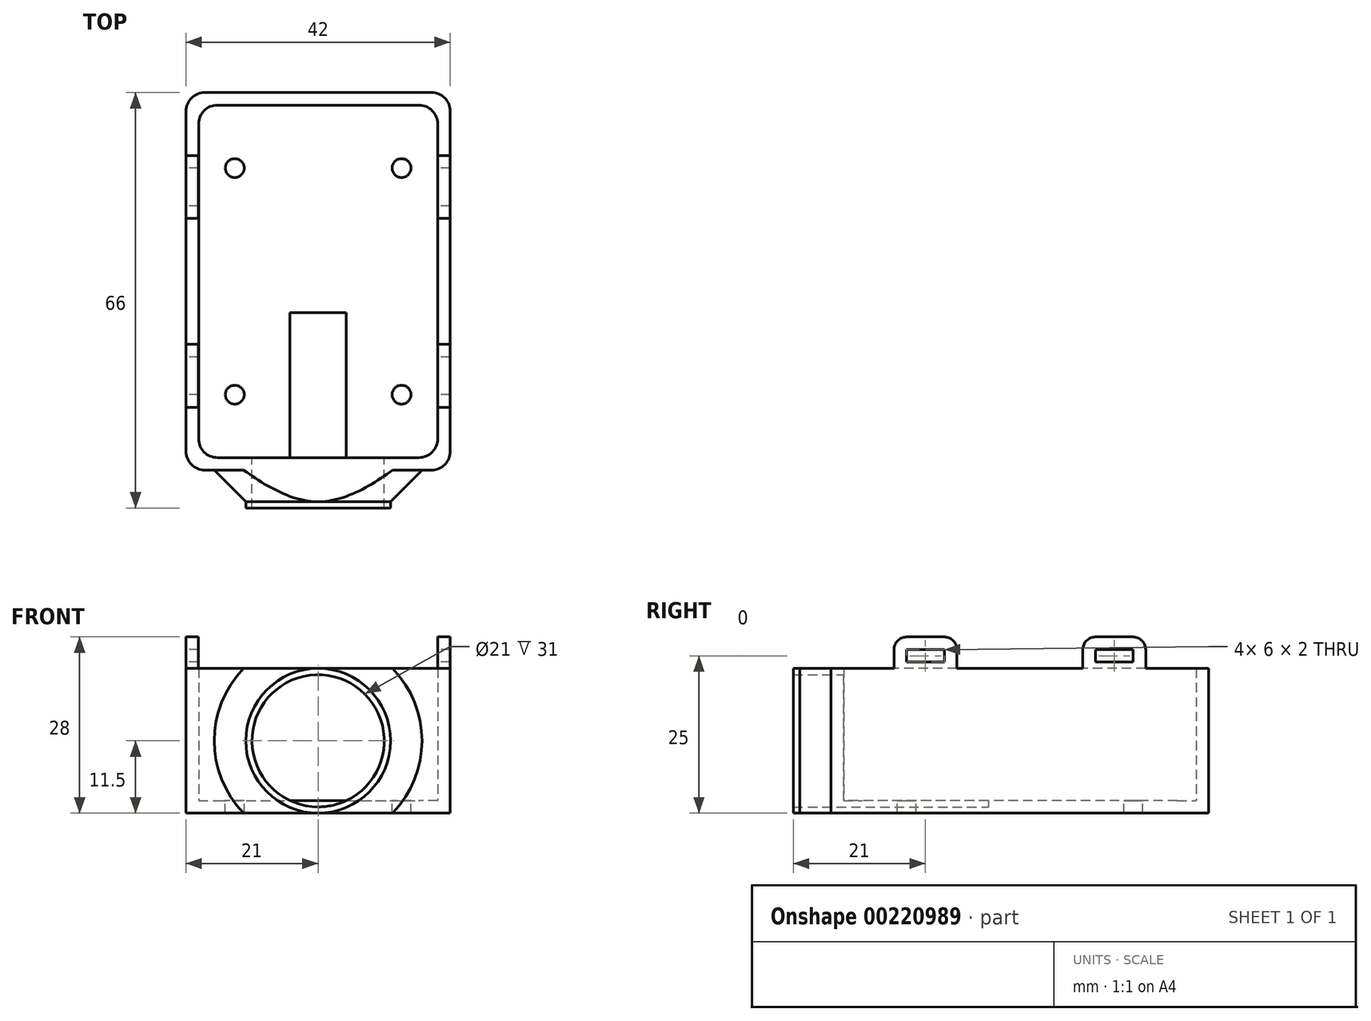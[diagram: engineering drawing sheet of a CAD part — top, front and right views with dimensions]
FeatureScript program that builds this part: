
annotation { "Feature Type Name" : "Feature", "Feature Type Description" : "" }
export const myFeature = defineFeature(function(context is Context, id is Id, definition is map)
    precondition{}
    {
        {
            assignVariable(context, id + "F0", {"name" : "defaultThickness", "anyValue" : 2});
        }
        {
            assignVariable(context, id + "F1", {"name" : "depth", "anyValue" : 21});
        }
        {
            assignVariable(context, id + "F2", {"name" : "camProtrusion", "anyValue" : 12});
        }
        {
            var Q0;
            Q0=qCreatedBy(makeId("Top.planeOp"),FACE);
            var sketch = newSketch(context, id + "F3", { "sketchPlane" : qUnion([Q0])});
            skLineSegment(sketch, "E0.bottom", {"start": v(-16, 28) * mm, "end": v(16, 28) * mm});
            skLineSegment(sketch, "E0.top", {"start": v(-16, -28) * mm, "end": v(16, -28) * mm});
            skLineSegment(sketch, "E0.left", {"start": v(-19, 25) * mm, "end": v(-19, -25) * mm});
            skLineSegment(sketch, "E0.right", {"start": v(19, 25) * mm, "end": v(19, -25) * mm});
            skPoint(sketch, "E0.middle", {"position": v(0, 0) * mm});
            skLineSegment(sketch, "E1.bottom", {"start": v(-18, 30) * mm, "end": v(18, 30) * mm});
            skLineSegment(sketch, "E1.top", {"start": v(-18, -30) * mm, "end": v(18, -30) * mm});
            skLineSegment(sketch, "E1.left", {"start": v(-21, 27) * mm, "end": v(-21, -27) * mm});
            skLineSegment(sketch, "E1.right", {"start": v(21, 27) * mm, "end": v(21, -27) * mm});
            skPoint(sketch, "E2.visualSharp", {"position": v(-19, 28) * mm});
            skArc(sketch, "E2.filletArc", {"start": v(-16, 28) * mm, "mid": v(-18.12, 27.12) * mm, "end": v(-19, 25) * mm});
            skPoint(sketch, "E3.visualSharp", {"position": v(19, 28) * mm});
            skArc(sketch, "E3.filletArc", {"start": v(19, 25) * mm, "mid": v(18.12, 27.12) * mm, "end": v(16, 28) * mm});
            skPoint(sketch, "E4.visualSharp", {"position": v(19, -28) * mm});
            skArc(sketch, "E4.filletArc", {"start": v(16, -28) * mm, "mid": v(18.12, -27.12) * mm, "end": v(19, -25) * mm});
            skPoint(sketch, "E5.visualSharp", {"position": v(-19, -28) * mm});
            skArc(sketch, "E5.filletArc", {"start": v(-19, -25) * mm, "mid": v(-18.12, -27.12) * mm, "end": v(-16, -28) * mm});
            skPoint(sketch, "E6.visualSharp", {"position": v(-21, -30) * mm});
            skArc(sketch, "E6.filletArc", {"start": v(-21, -27) * mm, "mid": v(-20.12, -29.12) * mm, "end": v(-18, -30) * mm});
            skPoint(sketch, "E7.visualSharp", {"position": v(21, -30) * mm});
            skArc(sketch, "E7.filletArc", {"start": v(18, -30) * mm, "mid": v(20.12, -29.12) * mm, "end": v(21, -27) * mm});
            skPoint(sketch, "E8.visualSharp", {"position": v(21, 30) * mm});
            skArc(sketch, "E8.filletArc", {"start": v(21, 27) * mm, "mid": v(20.12, 29.12) * mm, "end": v(18, 30) * mm});
            skPoint(sketch, "E9.visualSharp", {"position": v(-21, 30) * mm});
            skArc(sketch, "E9.filletArc", {"start": v(-18, 30) * mm, "mid": v(-20.12, 29.12) * mm, "end": v(-21, 27) * mm});
            skSolve(sketch);
        }
        {
            var Q0;
            Q0=makeQuery(id+"F3.imprint","IMPRINT",FACE,{"disambiguationData":[TD([[makeQuery(id+"F3.imprint","IMPRINT",EDGE,{"derivedFrom":sQuery(id+"F3.wireOp",EDGE,"E0.bottom")}),1.0]])]});
            extrude(context, id + "F4", {"entities" : qUnion([Q0]), "depth" : (getVariable(context, 'depth') + getVariable(context, 'defaultThickness')) * mm});
        }
        {
            var Q0;
            Q0=makeQuery(id+"F3.imprint","IMPRINT",FACE,{"disambiguationData":[TD([[makeQuery(id+"F3.imprint","IMPRINT",EDGE,{"derivedFrom":sQuery(id+"F3.wireOp",EDGE,"E0.bottom")}),-1.0]])]});
            extrude(context, id + "F5", {"entities" : qUnion([Q0]), "operationType" : NewBodyOperationType.ADD, "depth" : (getVariable(context, 'defaultThickness')) * mm});
        }
        {
            var Q0;
            Q0=makeQuery(id+"F4.opExtrude","SWEPT_FACE",FACE,{"disambiguationData":[OSD([sQuery(id+"F3.wireOp",EDGE,"E1.top")])]});
            var sketch = newSketch(context, id + "F6", { "sketchPlane" : qUnion([Q0])});
            skCircle(sketch, "E10", {"center": v(0, 11.5) * mm, "radius": 10.5 * mm});
            skCircle(sketch, "E11", {"center": v(0, 11.5) * mm, "radius": 11.5 * mm});
            skSolve(sketch);
        }
        {
            var Q0;
            Q0 = qSketchRegion(id + "F6", true);
            extrude(context, id + "F7", {"entities" : qUnion([Q0]), "operationType" : NewBodyOperationType.ADD, "depth" : (getVariable(context, 'camProtrusion') / 2) * mm});
        }
        {
            var Q0;
            Q0=makeQuery(id+"F7.boolean.opBoolean","SPLIT",FACE,{"disambiguationData":[TD([makeQuery(id+"F7.opExtrude","SWEPT_FACE",FACE,{"disambiguationData":[OSD([sQuery(id+"F6.wireOp",EDGE,"E10")])]})])],"derivedFrom":makeQuery(id+"F4.opExtrude","SWEPT_FACE",FACE,{"disambiguationData":[OSD([sQuery(id+"F3.wireOp",EDGE,"E1.top")])]})});
            extrude(context, id + "F8", {"entities" : qUnion([Q0]), "operationType" : NewBodyOperationType.REMOVE, "oppositeDirection" : true, "depth" : 25 * mm});
        }
        {
            var Q0;
            Q0=makeQuery(id+"F7.boolean.opBoolean","SPLIT",EDGE,{"disambiguationData":[OD(1.0)],"derivedFrom":makeQuery(id+"F7.opExtrude","CAP_EDGE",EDGE,{"disambiguationData":[OSD([sQuery(id+"F6.wireOp",EDGE,"E11")])],"isStart":true})});
            chamfer(context, id + "F9", {"entities" : qUnion([Q0]), "width" : 5 * mm, "tangentPropagation" : true});
        }
        {
            var Q0;
            Q0=makeQuery(id+"F5.opExtrude","CAP_FACE",FACE,{"disambiguationData":[OSD([sQuery(id+"F3.wireOp",EDGE,"E0.bottom"),sQuery(id+"F3.wireOp",EDGE,"E0.top"),sQuery(id+"F3.wireOp",EDGE,"E0.left"),sQuery(id+"F3.wireOp",EDGE,"E0.right"),sQuery(id+"F3.wireOp",EDGE,"E2.filletArc"),sQuery(id+"F3.wireOp",EDGE,"E3.filletArc"),sQuery(id+"F3.wireOp",EDGE,"E4.filletArc"),sQuery(id+"F3.wireOp",EDGE,"E5.filletArc")])],"isStart":false});
            var sketch = newSketch(context, id + "F10", { "sketchPlane" : qUnion([Q0])});
            skCircle(sketch, "E12", {"center": v(-13.25, 18) * mm, "radius": 1.5 * mm});
            skCircle(sketch, "E13", {"center": v(-13.25, -18) * mm, "radius": 1.5 * mm});
            skCircle(sketch, "E14", {"center": v(13.25, 18) * mm, "radius": 1.5 * mm});
            skCircle(sketch, "E15", {"center": v(13.25, -18) * mm, "radius": 1.5 * mm});
            skPoint(sketch, "E16", {"position": v(-0.21, -18) * mm});
            skLineSegment(sketch, "E17", {"start": v(-13.25, 18) * mm, "end": v(0, 18) * mm, "construction": true});
            skLineSegment(sketch, "E18", {"start": v(0, 18) * mm, "end": v(13.25, 18) * mm, "construction": true});
            skLineSegment(sketch, "E19", {"start": v(-13.25, -18) * mm, "end": v(0, -18) * mm, "construction": true});
            skLineSegment(sketch, "E20", {"start": v(0, -18) * mm, "end": v(13.25, -18) * mm, "construction": true});
            skSolve(sketch);
        }
        {
            var Q0;
            Q0 = qSketchRegion(id + "F10", true);
            extrude(context, id + "F11", {"entities" : qUnion([Q0]), "operationType" : NewBodyOperationType.REMOVE, "endBound" : BoundingType.THROUGH_ALL, "oppositeDirection" : true, "depth" : 25 * mm});
        }
        {
            var Q0;
            Q0=makeQuery(id+"F4.opExtrude","CAP_FACE",FACE,{"disambiguationData":[OSD([sQuery(id+"F3.wireOp",EDGE,"E0.bottom"),sQuery(id+"F3.wireOp",EDGE,"E0.top"),sQuery(id+"F3.wireOp",EDGE,"E0.left"),sQuery(id+"F3.wireOp",EDGE,"E0.right"),sQuery(id+"F3.wireOp",EDGE,"E1.bottom"),sQuery(id+"F3.wireOp",EDGE,"E1.top"),sQuery(id+"F3.wireOp",EDGE,"E1.left"),sQuery(id+"F3.wireOp",EDGE,"E1.right"),sQuery(id+"F3.wireOp",EDGE,"E2.filletArc"),sQuery(id+"F3.wireOp",EDGE,"E3.filletArc"),sQuery(id+"F3.wireOp",EDGE,"E4.filletArc"),sQuery(id+"F3.wireOp",EDGE,"E5.filletArc"),sQuery(id+"F3.wireOp",EDGE,"E6.filletArc"),sQuery(id+"F3.wireOp",EDGE,"E7.filletArc"),sQuery(id+"F3.wireOp",EDGE,"E8.filletArc"),sQuery(id+"F3.wireOp",EDGE,"E9.filletArc")])],"isStart":false});
            var sketch = newSketch(context, id + "F12", { "sketchPlane" : qUnion([Q0])});
            skLineSegment(sketch, "E21.bottom", {"start": v(-21, 20) * mm, "end": v(-19.01, 20) * mm});
            skLineSegment(sketch, "E21.top", {"start": v(-21, 10) * mm, "end": v(-19.01, 10) * mm});
            skLineSegment(sketch, "E21.left", {"start": v(-21, 20) * mm, "end": v(-21, 10) * mm});
            skLineSegment(sketch, "E21.right", {"start": v(-19.01, 20) * mm, "end": v(-19.01, 10) * mm});
            skPoint(sketch, "E21.middle", {"position": v(-20, 15) * mm});
            skLineSegment(sketch, "E22.bottom", {"start": v(-21, -10) * mm, "end": v(-19.01, -10) * mm});
            skLineSegment(sketch, "E22.top", {"start": v(-21, -20) * mm, "end": v(-19.01, -20) * mm});
            skLineSegment(sketch, "E22.left", {"start": v(-21, -10) * mm, "end": v(-21, -20) * mm});
            skLineSegment(sketch, "E22.right", {"start": v(-19.01, -10) * mm, "end": v(-19.01, -20) * mm});
            skPoint(sketch, "E22.middle", {"position": v(-20, -15) * mm});
            skLineSegment(sketch, "E23", {"start": v(-20, 15) * mm, "end": v(-20, 0) * mm, "construction": true});
            skLineSegment(sketch, "E24", {"start": v(-20, 0) * mm, "end": v(-20, -15) * mm, "construction": true});
            skLineSegment(sketch, "E25.MirrorCS", {"start": v(21, 20) * mm, "end": v(21, 10) * mm});
            skLineSegment(sketch, "E26.MirrorCS", {"start": v(21, 20) * mm, "end": v(19.01, 20) * mm});
            skLineSegment(sketch, "E27.MirrorCS", {"start": v(21, -20) * mm, "end": v(19.01, -20) * mm});
            skLineSegment(sketch, "E28.MirrorCS", {"start": v(21, 10) * mm, "end": v(19.01, 10) * mm});
            skLineSegment(sketch, "E29.MirrorCS", {"start": v(21, -10) * mm, "end": v(19.01, -10) * mm});
            skPoint(sketch, "E30.MirrorP", {"position": v(20, 15) * mm});
            skLineSegment(sketch, "E31.MirrorCS", {"start": v(20, 0) * mm, "end": v(20, -15) * mm, "construction": true});
            skLineSegment(sketch, "E32.MirrorCS", {"start": v(20, 15) * mm, "end": v(20, 0) * mm, "construction": true});
            skLineSegment(sketch, "E33.MirrorCS", {"start": v(19.01, -10) * mm, "end": v(19.01, -20) * mm});
            skLineSegment(sketch, "E34.MirrorCS", {"start": v(21, -10) * mm, "end": v(21, -20) * mm});
            skPoint(sketch, "E35.MirrorP", {"position": v(20, -15) * mm});
            skLineSegment(sketch, "E36.MirrorCS", {"start": v(19.01, 20) * mm, "end": v(19.01, 10) * mm});
            skSolve(sketch);
        }
        {
            var Q0;
            Q0 = qSketchRegion(id + "F12", true);
            extrude(context, id + "F13", {"entities" : qUnion([Q0]), "operationType" : NewBodyOperationType.ADD, "depth" : 5 * mm});
        }
        {
            var Q0;
            Q0=makeQuery(id+"F13.opExtrude","CAP_EDGE",EDGE,{"disambiguationData":[OSD([sQuery(id+"F12.wireOp",EDGE,"E22.top")])],"isStart":false});
            var Q1;
            Q1=makeQuery(id+"F13.opExtrude","CAP_EDGE",EDGE,{"disambiguationData":[OSD([sQuery(id+"F12.wireOp",EDGE,"E22.bottom")])],"isStart":false});
            var Q2;
            Q2=makeQuery(id+"F13.opExtrude","CAP_EDGE",EDGE,{"disambiguationData":[OSD([sQuery(id+"F12.wireOp",EDGE,"E21.top")])],"isStart":false});
            var Q3;
            Q3=makeQuery(id+"F13.opExtrude","CAP_EDGE",EDGE,{"disambiguationData":[OSD([sQuery(id+"F12.wireOp",EDGE,"E21.bottom")])],"isStart":false});
            var Q4;
            Q4=makeQuery(id+"F13.opExtrude","CAP_EDGE",EDGE,{"disambiguationData":[OSD([sQuery(id+"F12.wireOp",EDGE,"E26.MirrorCS")])],"isStart":false});
            var Q5;
            Q5=makeQuery(id+"F13.opExtrude","CAP_EDGE",EDGE,{"disambiguationData":[OSD([sQuery(id+"F12.wireOp",EDGE,"E28.MirrorCS")])],"isStart":false});
            var Q6;
            Q6=makeQuery(id+"F13.opExtrude","CAP_EDGE",EDGE,{"disambiguationData":[OSD([sQuery(id+"F12.wireOp",EDGE,"E29.MirrorCS")])],"isStart":false});
            var Q7;
            Q7=makeQuery(id+"F13.opExtrude","CAP_EDGE",EDGE,{"disambiguationData":[OSD([sQuery(id+"F12.wireOp",EDGE,"E27.MirrorCS")])],"isStart":false});
            fillet(context, id + "F14", {"entities" : qUnion([Q0, Q1, Q2, Q3, Q4, Q5, Q6, Q7]), "radius" : 2 * mm, "tangentPropagation" : true, "allowEdgeOverflow" : false});
        }
        {
            var Q0;
            Q0=makeQuery(id+"F13.boolean.opBoolean","MERGE",FACE,{"derivedFrom":[makeQuery(id+"F4.opExtrude","SWEPT_FACE",FACE,{"disambiguationData":[OSD([sQuery(id+"F3.wireOp",EDGE,"E1.left")])]}),makeQuery(id+"F13.opExtrude","SWEPT_FACE",FACE,{"disambiguationData":[OSD([sQuery(id+"F12.wireOp",EDGE,"E21.left")])]}),makeQuery(id+"F13.opExtrude","SWEPT_FACE",FACE,{"disambiguationData":[OSD([sQuery(id+"F12.wireOp",EDGE,"E22.left")])]})]});
            var sketch = newSketch(context, id + "F15", { "sketchPlane" : qUnion([Q0])});
            skLineSegment(sketch, "E37.bottom", {"start": v(-18, 26) * mm, "end": v(-12, 26) * mm});
            skLineSegment(sketch, "E37.top", {"start": v(-18, 24) * mm, "end": v(-12, 24) * mm});
            skLineSegment(sketch, "E37.left", {"start": v(-18, 26) * mm, "end": v(-18, 24) * mm});
            skLineSegment(sketch, "E37.right", {"start": v(-12, 26) * mm, "end": v(-12, 24) * mm});
            skPoint(sketch, "E37.middle", {"position": v(-15, 25) * mm});
            skPoint(sketch, "E37.middle.positionSnap0", {"position": v(-15, 28) * mm});
            skPoint(sketch, "E37.centerSnap0", {"position": v(-15, 28) * mm});
            skLineSegment(sketch, "E38.MirrorCS", {"start": v(18, 26) * mm, "end": v(12, 26) * mm});
            skLineSegment(sketch, "E39.MirrorCS", {"start": v(12, 26) * mm, "end": v(12, 24) * mm});
            skLineSegment(sketch, "E40.MirrorCS", {"start": v(18, 24) * mm, "end": v(12, 24) * mm});
            skLineSegment(sketch, "E41.MirrorCS", {"start": v(18, 26) * mm, "end": v(18, 24) * mm});
            skSolve(sketch);
        }
        {
            var Q0;
            Q0 = qSketchRegion(id + "F15", true);
            extrude(context, id + "F16", {"entities" : qUnion([Q0]), "operationType" : NewBodyOperationType.REMOVE, "endBound" : BoundingType.THROUGH_ALL, "oppositeDirection" : true, "depth" : 25 * mm});
        }
    });
